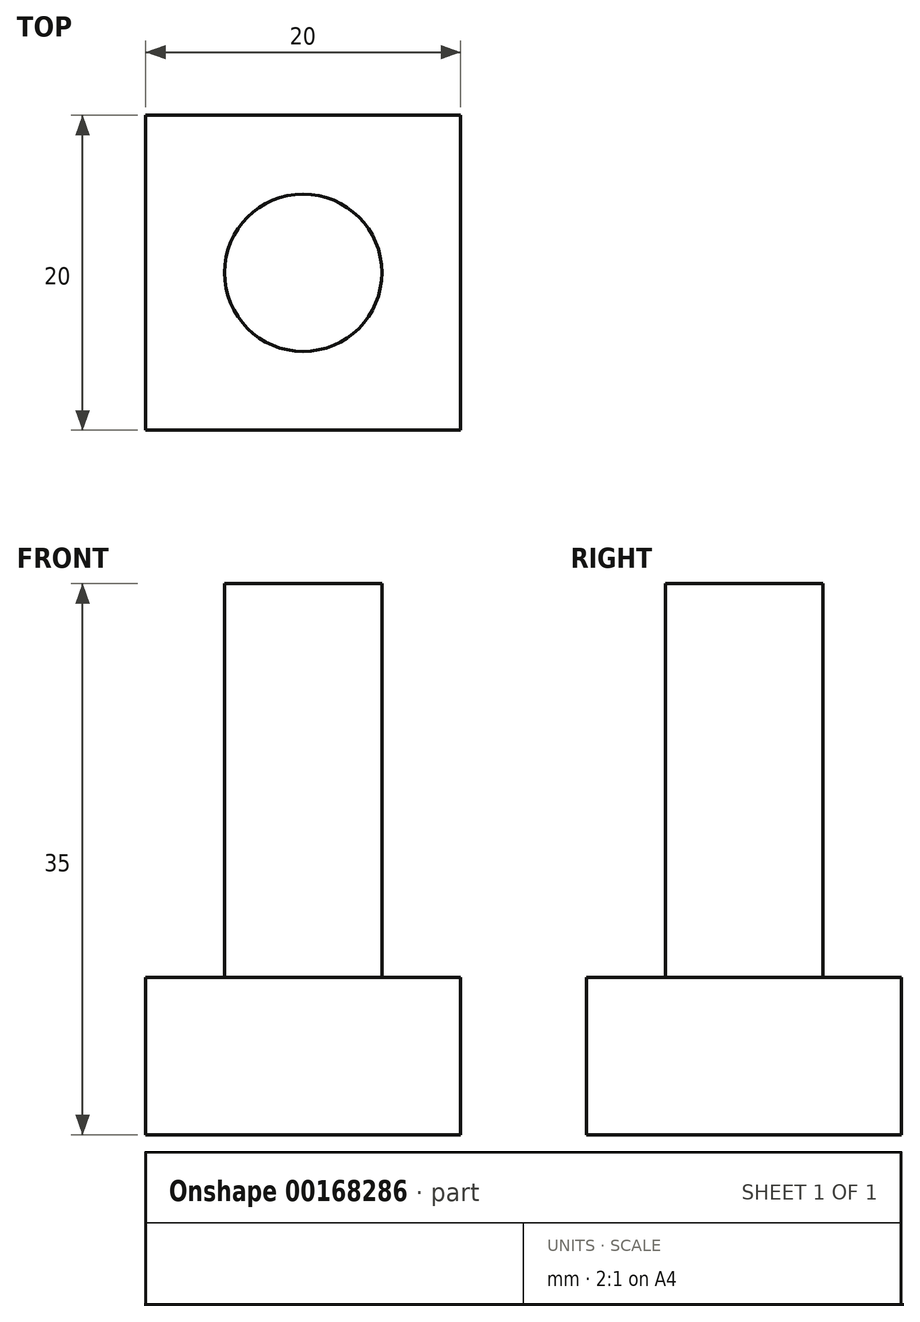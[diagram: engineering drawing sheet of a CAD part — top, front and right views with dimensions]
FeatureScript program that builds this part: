
annotation { "Feature Type Name" : "Feature", "Feature Type Description" : "" }
export const myFeature = defineFeature(function(context is Context, id is Id, definition is map)
    precondition{}
    {
        {
            var Q0;
            Q0=qCreatedBy(makeId("Top.planeOp"),FACE);
            var sketch = newSketch(context, id + "F0", { "sketchPlane" : qUnion([Q0])});
            skLineSegment(sketch, "E0.bottom", {"start": v(10, 10) * mm, "end": v(-10, 10) * mm});
            skLineSegment(sketch, "E0.top", {"start": v(10, -10) * mm, "end": v(-10, -10) * mm});
            skLineSegment(sketch, "E0.left", {"start": v(10, 10) * mm, "end": v(10, -10) * mm});
            skLineSegment(sketch, "E0.right", {"start": v(-10, 10) * mm, "end": v(-10, -10) * mm});
            skPoint(sketch, "E0.middle", {"position": v(0, 0) * mm});
            skSolve(sketch);
        }
        {
            var Q0;
            Q0=makeQuery(id+"F0.imprint","IMPRINT",FACE,{"disambiguationData":[TD([[makeQuery(id+"F0.imprint","IMPRINT",EDGE,{"derivedFrom":sQuery(id+"F0.wireOp",EDGE,"E0.bottom")}),1.0]])]});
            extrude(context, id + "F1", {"entities" : qUnion([Q0]), "depth" : 10 * mm});
        }
        {
            var Q0;
            Q0=makeQuery(id+"F1.opExtrude","CAP_FACE",FACE,{"disambiguationData":[OSD([sQuery(id+"F0.wireOp",EDGE,"E0.bottom"),sQuery(id+"F0.wireOp",EDGE,"E0.top"),sQuery(id+"F0.wireOp",EDGE,"E0.left"),sQuery(id+"F0.wireOp",EDGE,"E0.right")])],"isStart":false});
            var sketch = newSketch(context, id + "F2", { "sketchPlane" : qUnion([Q0])});
            skCircle(sketch, "E1", {"center": v(0, 0) * mm, "radius": 5 * mm});
            skSolve(sketch);
        }
        {
            var Q0;
            Q0=qSketchRegion(id+"F2",true);
            extrude(context, id + "F3", {"entities" : qUnion([Q0]), "operationType" : NewBodyOperationType.ADD, "depth" : 25 * mm});
        }
    });
